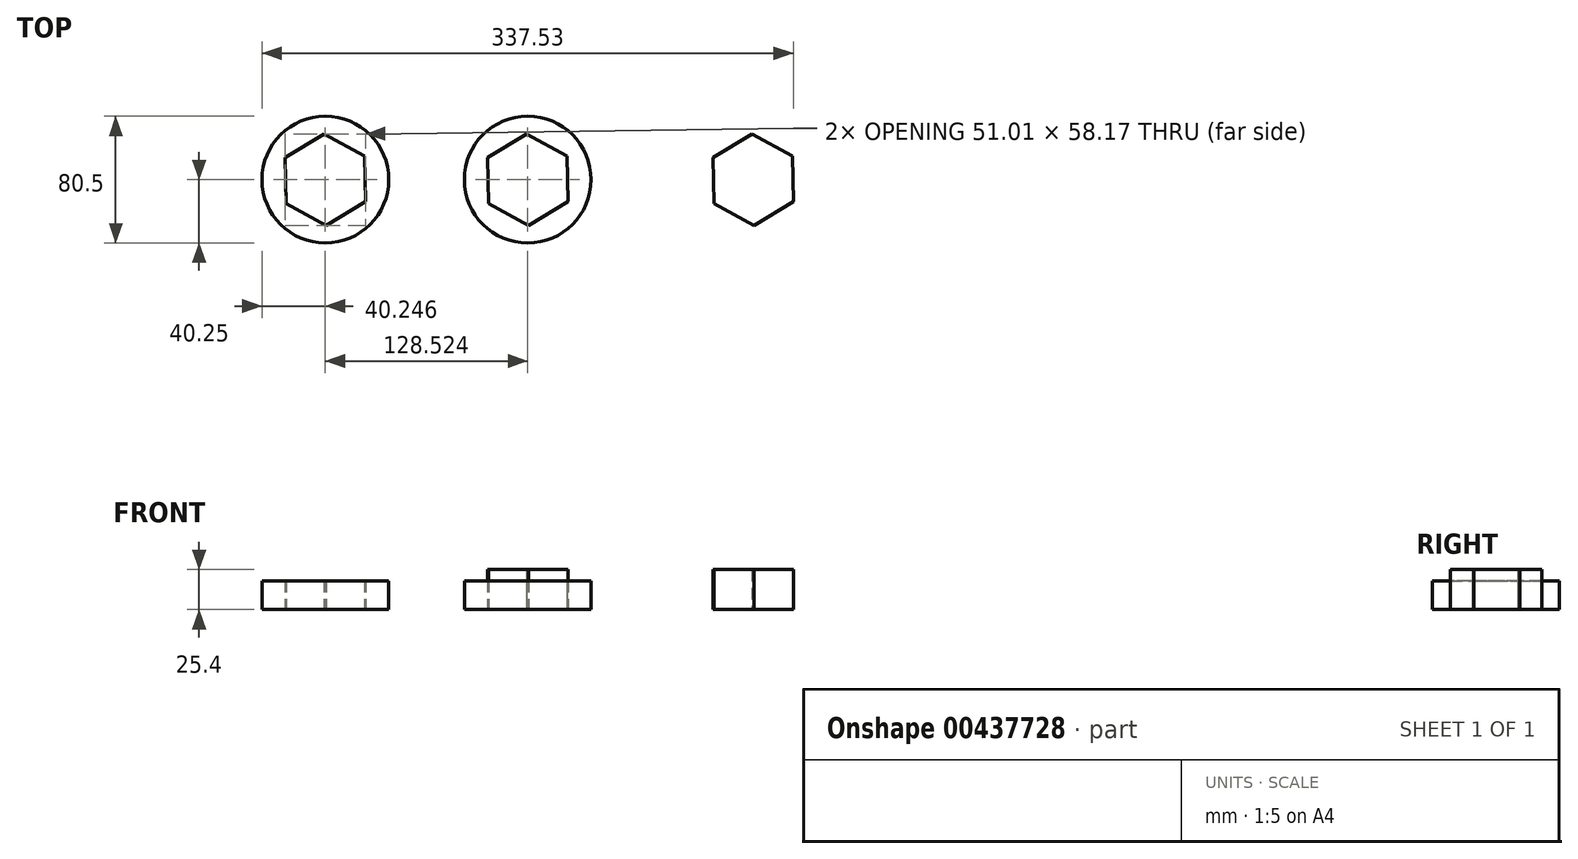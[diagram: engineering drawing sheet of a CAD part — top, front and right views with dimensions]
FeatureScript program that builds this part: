
annotation { "Feature Type Name" : "Feature", "Feature Type Description" : "" }
export const myFeature = defineFeature(function(context is Context, id is Id, definition is map)
    precondition{}
    {
        {
            var Q0;
            Q0=qCreatedBy(makeId("Top.planeOp"),FACE);
            var sketch = newSketch(context, id + "F0", { "sketchPlane" : qUnion([Q0])});
            skCircle(sketch, "E0.cCircle", {"center": v(0, 0) * mm, "radius": 25.2 * mm, "construction": true});
            skLineSegment(sketch, "E0.0", {"start": v(-0.63, 29.08) * mm, "end": v(24.87, 15.1) * mm});
            skLineSegment(sketch, "E0.1", {"start": v(24.87, 15.1) * mm, "end": v(25.5, -14) * mm});
            skLineSegment(sketch, "E0.2", {"start": v(25.5, -14) * mm, "end": v(0.63, -29.08) * mm});
            skLineSegment(sketch, "E0.3", {"start": v(0.63, -29.08) * mm, "end": v(-24.87, -15.1) * mm});
            skLineSegment(sketch, "E0.4", {"start": v(-24.87, -15.1) * mm, "end": v(-25.5, 14) * mm});
            skLineSegment(sketch, "E0.5", {"start": v(-25.5, 14) * mm, "end": v(-0.63, 29.08) * mm});
            skPoint(sketch, "E0.0.midPoint", {"position": v(12.12, 22.09) * mm});
            skSolve(sketch);
        }
        {
            var Q0;
            Q0=makeQuery(id+"F0.imprint","IMPRINT",FACE,{"disambiguationData":[TD([[makeQuery(id+"F0.imprint","IMPRINT",EDGE,{"derivedFrom":sQuery(id+"F0.wireOp",EDGE,"E0.0")}),-1.0]])]});
            extrude(context, id + "F1", {"entities" : qUnion([Q0]), "depth" : 25.4 * mm});
        }
        {
            var Q0;
            Q0=qCreatedBy(makeId("Top.planeOp"),FACE);
            var sketch = newSketch(context, id + "F2", { "sketchPlane" : qUnion([Q0])});
            skCircle(sketch, "E1", {"center": v(0, 0) * mm, "radius": 40.25 * mm});
            skSolve(sketch);
        }
        {
            var Q0;
            Q0=makeQuery(id+"F2.imprint","IMPRINT",FACE,{"disambiguationData":[TD([[makeQuery(id+"F2.imprint","IMPRINT",EDGE,{"derivedFrom":sQuery(id+"F2.wireOp",EDGE,"E1")}),1.0]])]});
            extrude(context, id + "F3", {"entities" : qUnion([Q0]), "depth" : 18.29 * mm});
        }
        {
            var Q0;
            Q0=makeQuery(id+"F1.opExtrude","SWEPT_BODY",BODY,{"disambiguationData":[OSD([sQuery(id+"F0.wireOp",EDGE,"E0.0"),sQuery(id+"F0.wireOp",EDGE,"E0.1"),sQuery(id+"F0.wireOp",EDGE,"E0.2"),sQuery(id+"F0.wireOp",EDGE,"E0.3"),sQuery(id+"F0.wireOp",EDGE,"E0.4"),sQuery(id+"F0.wireOp",EDGE,"E0.5")])]});
            var Q1;
            Q1=makeQuery(id+"F3.opExtrude","SWEPT_BODY",BODY,{"disambiguationData":[OSD([sQuery(id+"F2.wireOp",EDGE,"E1")])]});
            booleanBodies(context, id + "F4", {"operationType" : BooleanOperationType.SUBTRACTION, "tools" : qUnion([Q0]), "targets" : qUnion([Q1]), "keepTools" : true});
        }
        {
            var Q0;
            Q0=makeQuery(id+"F1.opExtrude","SWEPT_BODY",BODY,{"disambiguationData":[OSD([sQuery(id+"F0.wireOp",EDGE,"E0.0"),sQuery(id+"F0.wireOp",EDGE,"E0.1"),sQuery(id+"F0.wireOp",EDGE,"E0.2"),sQuery(id+"F0.wireOp",EDGE,"E0.3"),sQuery(id+"F0.wireOp",EDGE,"E0.4"),sQuery(id+"F0.wireOp",EDGE,"E0.5")])]});
            transform(context, id + "F5", {"entities" : qUnion([Q0]), "transformType" : TransformType.TRANSLATION_3D, "dx" : 143.26 * mm, "dy" : 0 * mm, "dz" : 0 * mm, "makeCopy" : true});
        }
        {
            var Q0;
            Q0=makeQuery(id+"F3.opExtrude","SWEPT_BODY",BODY,{"disambiguationData":[OSD([sQuery(id+"F2.wireOp",EDGE,"E1")])]});
            transform(context, id + "F6", {"entities" : qUnion([Q0]), "transformType" : TransformType.TRANSLATION_3D, "dx" : -128.52 * mm, "dy" : 0 * mm, "dz" : 0 * mm, "makeCopy" : true});
        }
    });
